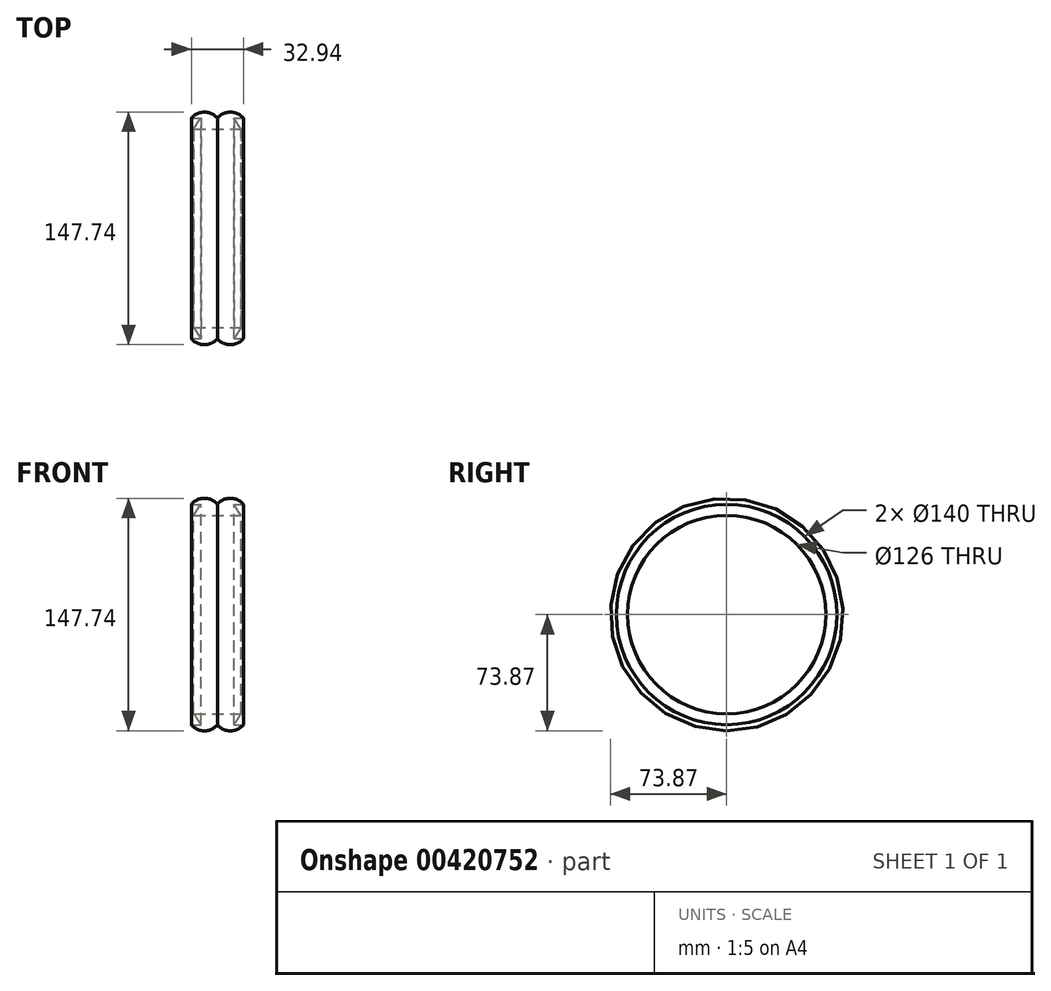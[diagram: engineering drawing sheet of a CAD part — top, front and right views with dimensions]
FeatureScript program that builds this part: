
annotation { "Feature Type Name" : "Feature", "Feature Type Description" : "" }
export const myFeature = defineFeature(function(context is Context, id is Id, definition is map)
    precondition{}
    {
        {
            var Q0;
            Q0=qCreatedBy(makeId("Front.planeOp"),FACE);
            var sketch = newSketch(context, id + "F0", { "sketchPlane" : qUnion([Q0])});
            skLineSegment(sketch, "E0.bottom", {"start": v(0, 0) * mm, "end": v(-42, 0) * mm});
            skLineSegment(sketch, "E1", {"start": v(-21, 0) * mm, "end": v(-21, -70) * mm, "construction": true});
            skPoint(sketch, "E2", {"position": v(-10.5, -70) * mm});
            skPoint(sketch, "E3", {"position": v(-31.5, -70) * mm});
            skPoint(sketch, "E4", {"position": v(-36, -63) * mm});
            skPoint(sketch, "E5", {"position": v(-6, -63) * mm});
            skLineSegment(sketch, "E6", {"start": v(-37.47, -70) * mm, "end": v(-31.5, -70) * mm});
            skLineSegment(sketch, "E7", {"start": v(-10.5, -70) * mm, "end": v(-6, -63) * mm});
            skLineSegment(sketch, "E8", {"start": v(-6, -63) * mm, "end": v(-36, -63) * mm});
            skLineSegment(sketch, "E9", {"start": v(-10.5, -70) * mm, "end": v(-4.53, -70) * mm});
            skLineSegment(sketch, "E10", {"start": v(-36, -63) * mm, "end": v(-31.5, -70) * mm});
            skArc(sketch, "E11", {"start": v(-37.47, -70) * mm, "mid": v(-29.24, -73.87) * mm, "end": v(-21, -70) * mm});
            skArc(sketch, "E12", {"start": v(-21, -70) * mm, "mid": v(-12.76, -73.87) * mm, "end": v(-4.53, -70) * mm});
            skSolve(sketch);
        }
        {
            var Q0;
            Q0=makeQuery(id+"F0.imprint","IMPRINT",FACE,{"disambiguationData":[TD([[makeQuery(id+"F0.imprint","IMPRINT",EDGE,{"derivedFrom":sQuery(id+"F0.wireOp",EDGE,"E6")}),-1.0]])]});
            var Q1;
            Q1=sQuery(id+"F0.wireOp",EDGE,"E0.bottom");
            revolve(context, id + "F1", {"entities" : qUnion([Q0]), "axis" : qUnion([Q1]), "revolveType" : RevolveType.FULL});
        }
    });
